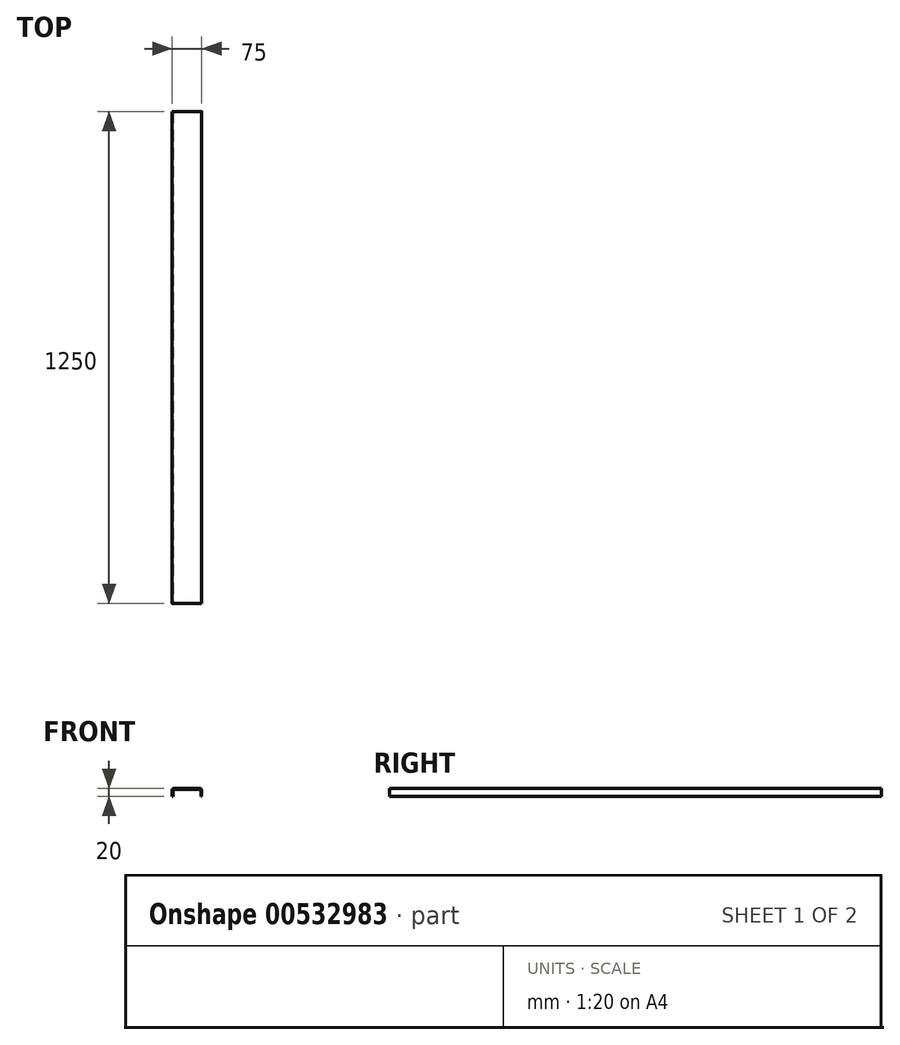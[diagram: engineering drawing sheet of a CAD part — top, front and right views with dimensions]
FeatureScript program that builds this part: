
annotation { "Feature Type Name" : "Feature", "Feature Type Description" : "" }
export const myFeature = defineFeature(function(context is Context, id is Id, definition is map)
    precondition{}
    {
        {
            var Q0;
            Q0=qCreatedBy(makeId("Front.planeOp"),FACE);
            var sketch = newSketch(context, id + "F0", { "sketchPlane" : qUnion([Q0])});
            skLineSegment(sketch, "E0", {"start": v(-95.5, 0) * mm, "end": v(-95.5, 16) * mm});
            skLineSegment(sketch, "E1", {"start": v(-91.5, 20) * mm, "end": v(-24.5, 20) * mm});
            skLineSegment(sketch, "E2", {"start": v(-20.5, 16) * mm, "end": v(-20.5, 0) * mm});
            skLineSegment(sketch, "E3.0", {"start": v(-22.5, 16) * mm, "end": v(-22.5, 0) * mm});
            skLineSegment(sketch, "E4.0", {"start": v(-91.5, 18) * mm, "end": v(-24.5, 18) * mm});
            skLineSegment(sketch, "E5.0", {"start": v(-93.5, 0) * mm, "end": v(-93.5, 16) * mm});
            skLineSegment(sketch, "E6", {"start": v(-95.5, 0) * mm, "end": v(-93.5, 0) * mm});
            skLineSegment(sketch, "E7", {"start": v(-20.5, 0) * mm, "end": v(-22.5, 0) * mm});
            skPoint(sketch, "E8.visualSharp", {"position": v(-22.5, 18) * mm});
            skArc(sketch, "E8.filletArc", {"start": v(-22.5, 16) * mm, "mid": v(-23.1, 17.41) * mm, "end": v(-24.5, 18) * mm});
            skPoint(sketch, "E9.visualSharp", {"position": v(-20.5, 20) * mm});
            skArc(sketch, "E9.filletArc", {"start": v(-20.5, 16) * mm, "mid": v(-21.68, 18.83) * mm, "end": v(-24.5, 20) * mm});
            skPoint(sketch, "E10.visualSharp", {"position": v(-95.5, 20) * mm});
            skArc(sketch, "E10.filletArc", {"start": v(-91.5, 20) * mm, "mid": v(-94.33, 18.83) * mm, "end": v(-95.5, 16) * mm});
            skPoint(sketch, "E11.visualSharp", {"position": v(-93.5, 18) * mm});
            skArc(sketch, "E11.filletArc", {"start": v(-91.5, 18) * mm, "mid": v(-92.92, 17.41) * mm, "end": v(-93.5, 16) * mm});
            skSolve(sketch);
        }
        {
            var Q0;
            Q0 = qSketchRegion(id + "F0", true);
            extrude(context, id + "F1", {"entities" : qUnion([Q0]), "oppositeDirection" : true, "depth" : 1250 * mm, "offsetDistance" : 25 * mm});
        }
    });
